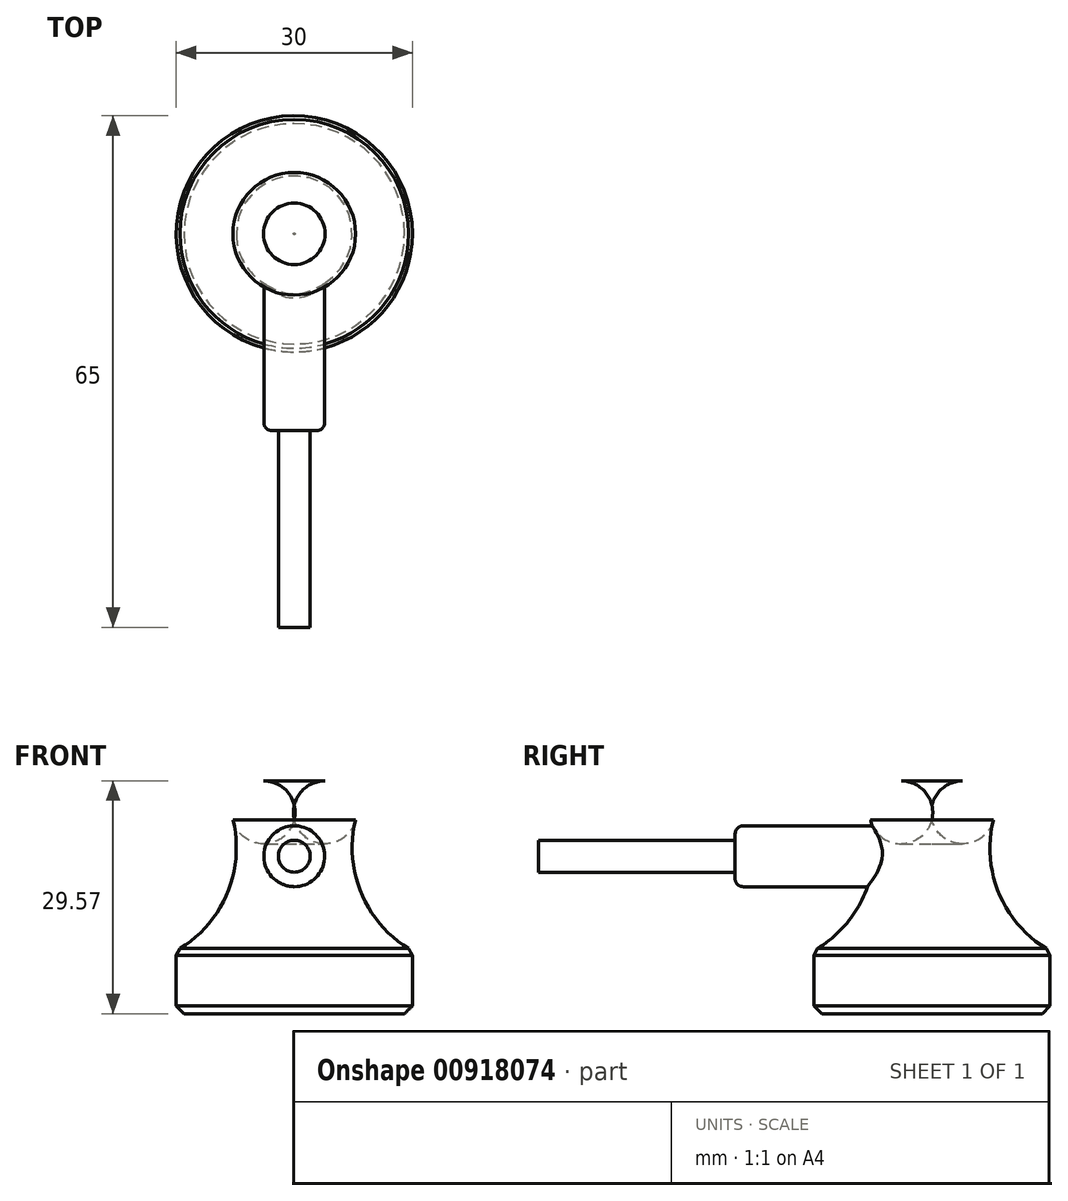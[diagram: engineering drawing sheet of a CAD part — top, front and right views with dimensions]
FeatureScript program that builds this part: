
annotation { "Feature Type Name" : "Feature", "Feature Type Description" : "" }
export const myFeature = defineFeature(function(context is Context, id is Id, definition is map)
    precondition{}
    {
        {
            var Q0;
            Q0=qCreatedBy(makeId("Front.planeOp"),FACE);
            var sketch = newSketch(context, id + "F0", { "sketchPlane" : qUnion([Q0])});
            skLineSegment(sketch, "E0", {"start": v(0, 39.24) * mm, "end": v(-10, 39.24) * mm});
            skArc(sketch, "E1", {"start": v(-15, 17.67) * mm, "mid": v(-7.75, 27.35) * mm, "end": v(-10, 39.24) * mm});
            skLineSegment(sketch, "E2", {"start": v(-15, 17.67) * mm, "end": v(-15, 9.67) * mm});
            skLineSegment(sketch, "E3", {"start": v(-15, 9.67) * mm, "end": v(0, 9.67) * mm});
            skLineSegment(sketch, "E4", {"start": v(0, 9.67) * mm, "end": v(0, 39.24) * mm});
            skSolve(sketch);
        }
        {
            var Q0;
            Q0 = qSketchRegion(id + "F0", true);
            var Q1;
            Q1=sQuery(id+"F0.wireOp",EDGE,"E4");
            revolve(context, id + "F1", {"surfaceOperationType" : NewSurfaceOperationType.NEW, "entities" : qUnion([Q0]), "axis" : qUnion([Q1]), "revolveType" : RevolveType.FULL});
        }
        {
            var Q0;
            Q0=qCreatedBy(makeId("Front.planeOp"),FACE);
            var sketch = newSketch(context, id + "F2", { "sketchPlane" : qUnion([Q0])});
            skCircle(sketch, "E5", {"center": v(0, 29.67) * mm, "radius": 3.86 * mm});
            skSolve(sketch);
        }
        {
            var Q0;
            Q0 = qSketchRegion(id + "F2", true);
            extrude(context, id + "F3", {"entities" : qUnion([Q0]), "operationType" : NewBodyOperationType.ADD, "depth" : 25 * mm, "offsetDistance" : 25 * mm});
        }
        {
            var Q0;
            Q0=makeQuery(id+"F3.opExtrude","CAP_FACE",FACE,{"disambiguationData":[OSD([sQuery(id+"F2.wireOp",EDGE,"E5")])],"isStart":false});
            var sketch = newSketch(context, id + "F4", { "sketchPlane" : qUnion([Q0])});
            skCircle(sketch, "E6", {"center": v(0, 29.67) * mm, "radius": 2.02 * mm});
            skSolve(sketch);
        }
        {
            var Q0;
            Q0 = qSketchRegion(id + "F4", true);
            extrude(context, id + "F5", {"entities" : qUnion([Q0]), "operationType" : NewBodyOperationType.ADD, "depth" : 25 * mm, "offsetDistance" : 25 * mm});
        }
        {
            var Q0;
            Q0=makeQuery(id+"F1.opRevolve","SWEPT_EDGE",EDGE,{"disambiguationData":[OSD([sQuery(id+"F0.wireOp",EDGE,"E0"),sQuery(id+"F0.wireOp",EDGE,"E1")])]});
            fillet(context, id + "F6", {"entities" : qUnion([Q0]), "radius" : 4 * mm, "tangentPropagation" : true, "allowEdgeOverflow" : false});
        }
        {
            var Q0;
            Q0=makeQuery(id+"F1.opRevolve","SWEPT_EDGE",EDGE,{"disambiguationData":[OSD([sQuery(id+"F0.wireOp",EDGE,"E1"),sQuery(id+"F0.wireOp",EDGE,"E2")])]});
            chamfer(context, id + "F7", {"entities" : qUnion([Q0]), "width" : 1 * mm, "tangentPropagation" : true});
        }
        {
            var Q0;
            Q0=makeQuery(id+"F3.opExtrude","CAP_EDGE",EDGE,{"disambiguationData":[OSD([sQuery(id+"F2.wireOp",EDGE,"E5")])],"isStart":false});
            fillet(context, id + "F8", {"entities" : qUnion([Q0]), "radius" : 1 * mm, "tangentPropagation" : true, "allowEdgeOverflow" : false});
        }
        {
            var Q0;
            Q0=makeQuery(id+"F1.opRevolve","SWEPT_EDGE",EDGE,{"disambiguationData":[OSD([sQuery(id+"F0.wireOp",EDGE,"E2"),sQuery(id+"F0.wireOp",EDGE,"E3")])]});
            chamfer(context, id + "F9", {"entities" : qUnion([Q0]), "width" : 1 * mm, "tangentPropagation" : true});
        }
    });
